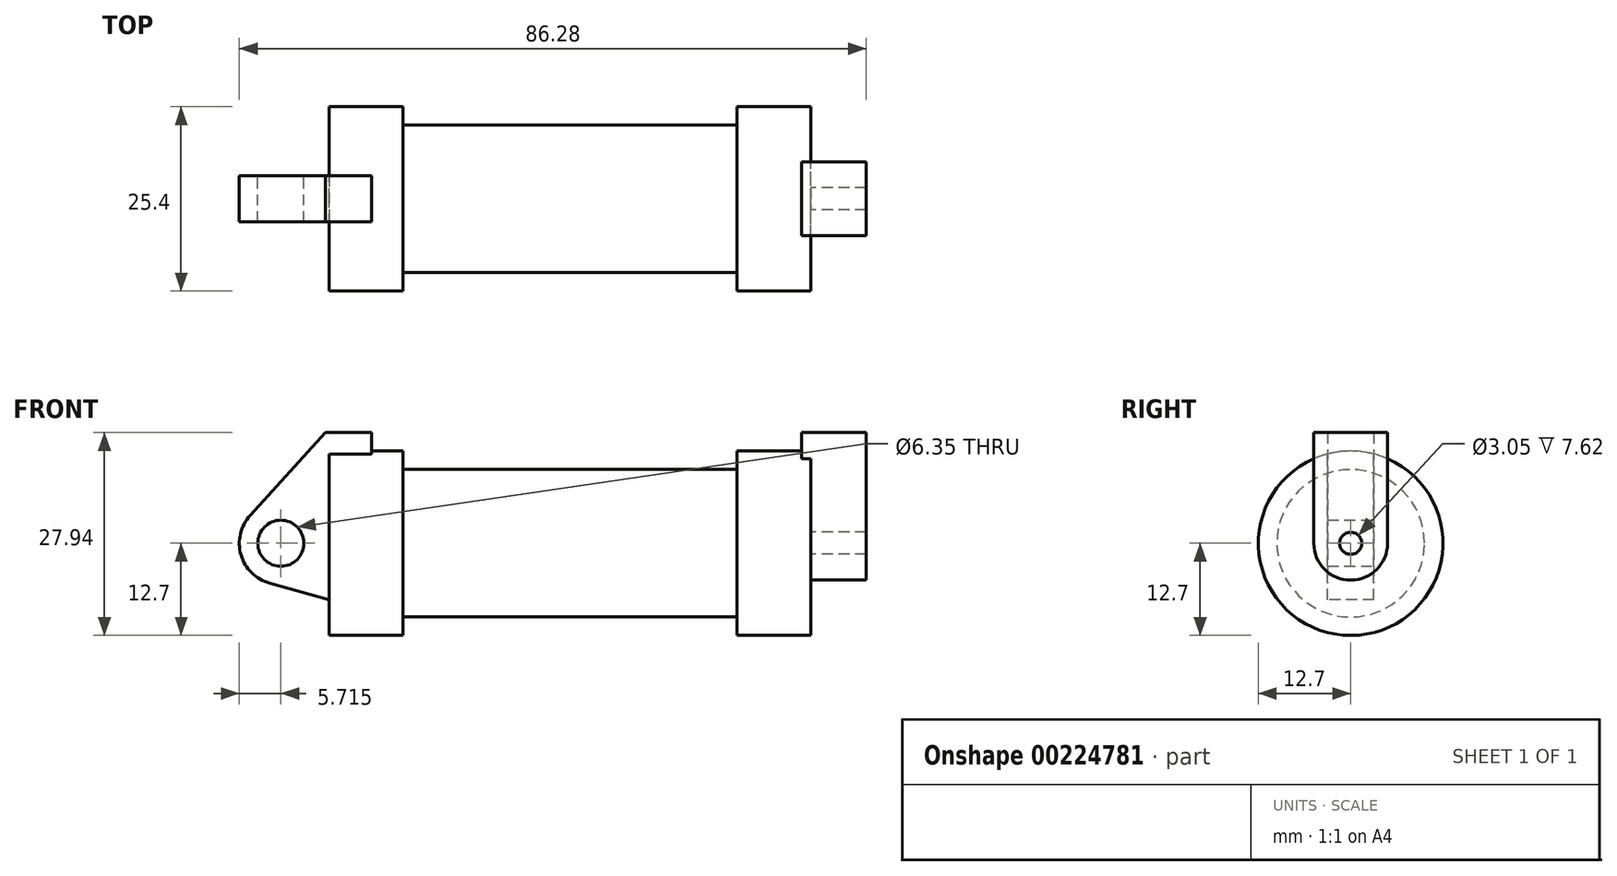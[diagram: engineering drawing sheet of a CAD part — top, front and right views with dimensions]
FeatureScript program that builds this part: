
annotation { "Feature Type Name" : "Feature", "Feature Type Description" : "" }
export const myFeature = defineFeature(function(context is Context, id is Id, definition is map)
    precondition{}
    {
        {
            var Q0;
            Q0=qCreatedBy(makeId("Front.planeOp"),FACE);
            var sketch = newSketch(context, id + "F0", { "sketchPlane" : qUnion([Q0])});
            skLineSegment(sketch, "E0", {"start": v(0, 0) * mm, "end": v(0, 12.7) * mm});
            skLineSegment(sketch, "E1", {"start": v(0, 12.7) * mm, "end": v(10.16, 12.7) * mm});
            skLineSegment(sketch, "E2", {"start": v(10.16, 12.7) * mm, "end": v(10.16, 10.16) * mm});
            skLineSegment(sketch, "E3", {"start": v(10.16, 10.16) * mm, "end": v(56.13, 10.16) * mm});
            skLineSegment(sketch, "E4", {"start": v(56.13, 10.16) * mm, "end": v(56.13, 12.7) * mm});
            skLineSegment(sketch, "E5", {"start": v(56.13, 12.7) * mm, "end": v(66.3, 12.7) * mm});
            skLineSegment(sketch, "E6", {"start": v(66.3, 12.7) * mm, "end": v(66.3, 0) * mm});
            skLineSegment(sketch, "E7", {"start": v(66.3, 0) * mm, "end": v(0, 0) * mm});
            skLineSegment(sketch, "E8", {"start": v(5.84, 15.24) * mm, "end": v(-0.5, 15.24) * mm});
            skLineSegment(sketch, "E9", {"start": v(-0.5, 15.24) * mm, "end": v(-10.88, 3.85) * mm});
            skLineSegment(sketch, "E10", {"start": v(0, 0) * mm, "end": v(-6.65, 0) * mm});
            skCircle(sketch, "E11", {"center": v(-6.65, 0) * mm, "radius": 5.72 * mm});
            skCircle(sketch, "E12", {"center": v(-6.65, 0) * mm, "radius": 3.18 * mm});
            skLineSegment(sketch, "E13", {"start": v(5.84, 15.24) * mm, "end": v(5.84, -9.4) * mm});
            skLineSegment(sketch, "E14", {"start": v(5.84, -9.4) * mm, "end": v(-8.18, -5.5) * mm});
            skSolve(sketch);
        }
        {
            var Q0;
            {var subQ3=sQuery(id+"F0.wireOp",EDGE,"E0");Q0=makeQuery(id+"F0.imprint","IMPRINT",FACE,{"disambiguationData":[TD([[makeQuery(id+"F0.imprint","IMPRINT",EDGE,{"derivedFrom":subQ3}),1.0]])]});}
            var Q1;
            {var subQ0=sQuery(id+"F0.wireOp",EDGE,"E14");Q1=makeQuery(id+"F0.imprint","IMPRINT",FACE,{"disambiguationData":[TD([[makeQuery(id+"F0.imprint","IMPRINT",EDGE,{"derivedFrom":subQ0}),-1.0]])]});}
            var Q2;
            {var subQ4=sQuery(id+"F0.wireOp",EDGE,"E12");Q2=makeQuery(id+"F0.imprint","IMPRINT",FACE,{"disambiguationData":[TD([[makeQuery(id+"F0.imprint","IMPRINT",EDGE,{"derivedFrom":subQ4}),-1.0]])]});}
            var Q3;
            {var subQ0=sQuery(id+"F0.wireOp",EDGE,"E0");Q3=makeQuery(id+"F0.imprint","IMPRINT",FACE,{"disambiguationData":[TD([[makeQuery(id+"F0.imprint","IMPRINT",EDGE,{"derivedFrom":subQ0}),-1.0]])]});}
            extrude(context, id + "F1", {"entities" : qUnion([Q0, Q1, Q2, Q3]), "depth" : 6.35 * mm, "symmetric" : true});
        }
        {
            var Q0;
            {var subQ0=sQuery(id+"F0.wireOp",EDGE,"E0");Q0=makeQuery(id+"F0.imprint","IMPRINT",FACE,{"disambiguationData":[TD([[makeQuery(id+"F0.imprint","IMPRINT",EDGE,{"derivedFrom":subQ0}),-1.0]])]});}
            var Q1;
            {var subQ0=sQuery(id+"F0.wireOp",EDGE,"E2");Q1=makeQuery(id+"F0.imprint","IMPRINT",FACE,{"disambiguationData":[TD([[makeQuery(id+"F0.imprint","IMPRINT",EDGE,{"derivedFrom":subQ0}),-1.0]])]});}
            var Q2;
            Q2=sQuery(id+"F0.wireOp",EDGE,"E7");
            revolve(context, id + "F2", {"operationType" : NewBodyOperationType.ADD, "entities" : qUnion([Q0, Q1]), "axis" : qUnion([Q2]), "revolveType" : RevolveType.FULL});
        }
        {
            var Q0;
            Q0=makeQuery(id+"F2.opRevolve","SWEPT_FACE",FACE,{"disambiguationData":[OSD([sQuery(id+"F0.wireOp",EDGE,"E6")])]});
            var sketch = newSketch(context, id + "F3", { "sketchPlane" : qUnion([Q0])});
            skCircle(sketch, "E15", {"center": v(0, 0) * mm, "radius": 1.52 * mm});
            skCircle(sketch, "E16", {"center": v(0, 0) * mm, "radius": 5.08 * mm});
            skLineSegment(sketch, "E17", {"start": v(0, 0) * mm, "end": v(-5.08, 0) * mm});
            skLineSegment(sketch, "E18", {"start": v(0, 0) * mm, "end": v(5.08, 0) * mm});
            skLineSegment(sketch, "E19.0", {"start": v(-3.18, 15.24) * mm, "end": v(3.17, 15.24) * mm});
            skLineSegment(sketch, "E20", {"start": v(-5.08, 0) * mm, "end": v(-5.08, 15.24) * mm});
            skPoint(sketch, "E20.endSnap0", {"position": v(0, 15.24) * mm});
            skLineSegment(sketch, "E21", {"start": v(5.08, 0) * mm, "end": v(5.08, 15.24) * mm});
            skLineSegment(sketch, "E22", {"start": v(5.08, 15.24) * mm, "end": v(-5.08, 15.24) * mm});
            skSolve(sketch);
        }
        {
            var Q0;
            {var subQ0=sQuery(id+"F3.wireOp",EDGE,"E22");var subQ1=sQuery(id+"F3.wireOp",EDGE,"E20");var subQ2=makeQuery(id+"F3.imprint","INTERSECT",VERTEX,{"derivedFrom":[subQ1,subQ0]});Q0=makeQuery(id+"F3.imprint","IMPRINT",FACE,{"disambiguationData":[TD([[makeQuery(id+"F3.imprint","IMPRINT",EDGE,{"disambiguationData":[TD([[subQ2,1.0]])],"derivedFrom":subQ0}),1.0]])]});}
            var Q1;
            {var subQ0=sQuery(id+"F3.wireOp",EDGE,"E20");var subQ1=sQuery(id+"F3.wireOp",EDGE,"E16");var subQ2=makeQuery(id+"F3.imprint","INTERSECT",VERTEX,{"derivedFrom":[subQ1,sQuery(id+"F3.wireOp",EDGE,"E17"),subQ0]});Q1=makeQuery(id+"F3.imprint","IMPRINT",FACE,{"disambiguationData":[TD([[makeQuery(id+"F3.imprint","IMPRINT",EDGE,{"disambiguationData":[TD([[subQ2,1.0]])],"derivedFrom":subQ1}),-1.0]])]});}
            var Q2;
            {var subQ0=sQuery(id+"F3.wireOp",EDGE,"E17");var subQ1=sQuery(id+"F3.wireOp",EDGE,"E15");var subQ2=makeQuery(id+"F3.imprint","INTERSECT",VERTEX,{"derivedFrom":[subQ1,subQ0]});Q2=makeQuery(id+"F3.imprint","IMPRINT",FACE,{"disambiguationData":[TD([[makeQuery(id+"F3.imprint","IMPRINT",EDGE,{"disambiguationData":[TD([[subQ2,1.0]])],"derivedFrom":subQ1}),-1.0]])]});}
            var Q3;
            {var subQ0=sQuery(id+"F3.wireOp",EDGE,"E17");var subQ1=sQuery(id+"F3.wireOp",EDGE,"E15");var subQ2=makeQuery(id+"F3.imprint","INTERSECT",VERTEX,{"derivedFrom":[subQ1,subQ0]});Q3=makeQuery(id+"F3.imprint","IMPRINT",FACE,{"disambiguationData":[TD([[makeQuery(id+"F3.imprint","IMPRINT",EDGE,{"disambiguationData":[TD([[subQ2,-1.0]])],"derivedFrom":subQ1}),-1.0]])]});}
            extrude(context, id + "F4", {"entities" : qUnion([Q0, Q1, Q2, Q3]), "operationType" : NewBodyOperationType.ADD, "depth" : 7.62 * mm});
        }
        {
            var Q0;
            Q0=makeQuery(id+"F4.opExtrude","CAP_FACE",FACE,{"disambiguationData":[OSD([sQuery(id+"F3.wireOp",EDGE,"E15"),sQuery(id+"F3.wireOp",EDGE,"E16"),sQuery(id+"F3.wireOp",EDGE,"E20"),sQuery(id+"F3.wireOp",EDGE,"E21"),sQuery(id+"F3.wireOp",EDGE,"E22")])],"isStart":true});
            extrude(context, id + "F5", {"entities" : qUnion([Q0]), "operationType" : NewBodyOperationType.ADD, "depth" : 1.27 * mm});
        }
    });
